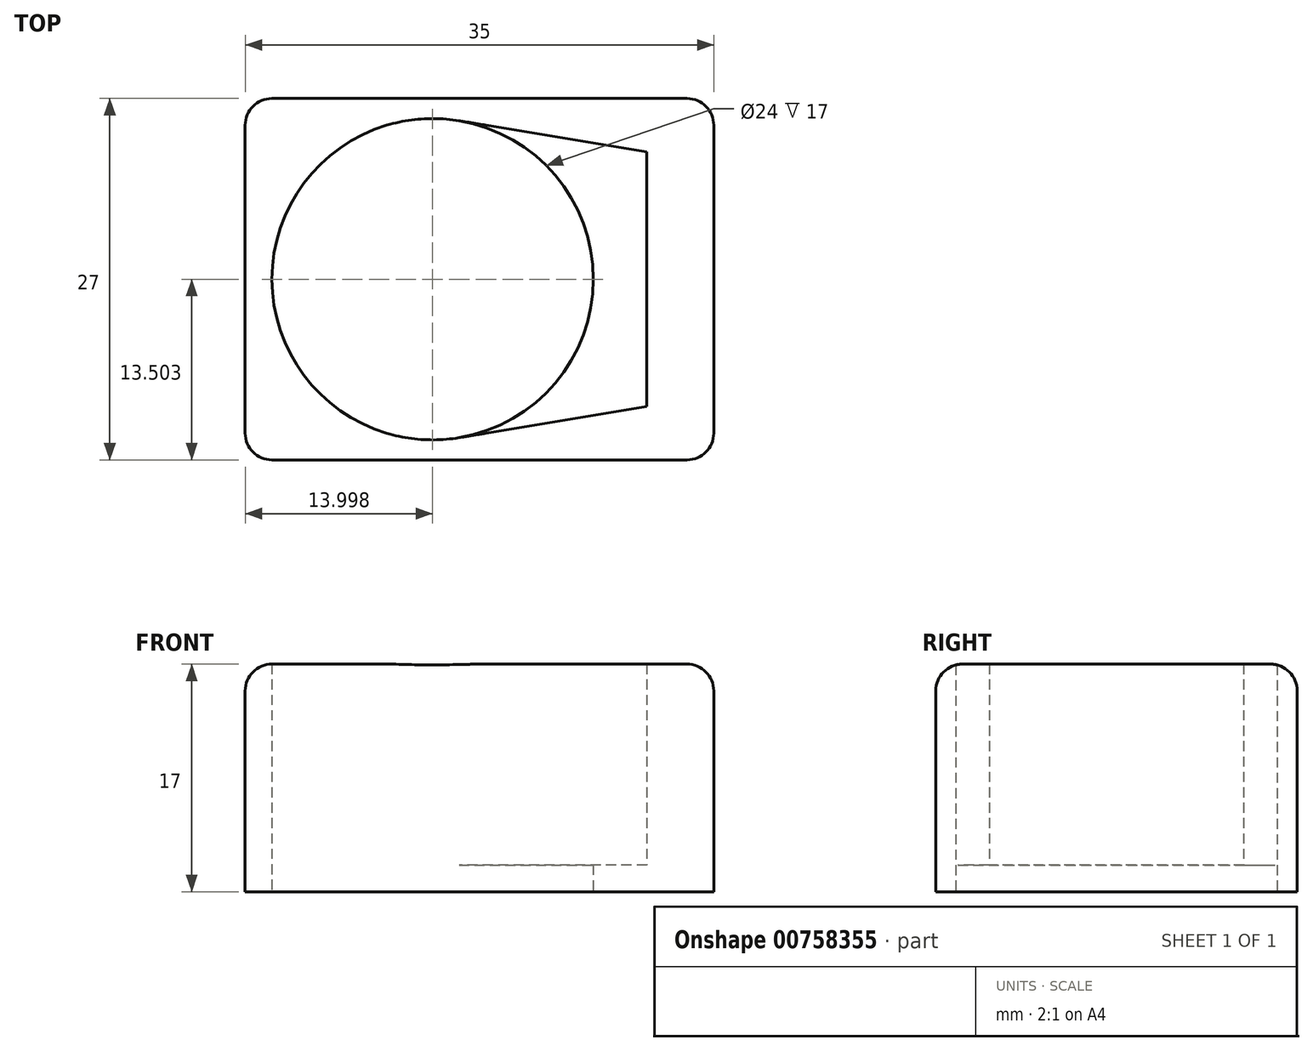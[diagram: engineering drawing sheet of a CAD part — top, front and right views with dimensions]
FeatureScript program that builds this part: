
annotation { "Feature Type Name" : "Feature", "Feature Type Description" : "" }
export const myFeature = defineFeature(function(context is Context, id is Id, definition is map)
    precondition{}
    {
        {
            var Q0;
            Q0=qCreatedBy(makeId("Top.planeOp"),FACE);
            var sketch = newSketch(context, id + "F0", { "sketchPlane" : qUnion([Q0])});
            skLineSegment(sketch, "E0", {"start": v(-0.7, 17.13) * mm, "end": v(-0.7, -1.87) * mm});
            skLineSegment(sketch, "E1", {"start": v(-0.7, 7.63) * mm, "end": v(-28.7, 7.63) * mm});
            skCircle(sketch, "E2", {"center": v(-16.7, 7.63) * mm, "radius": 12 * mm});
            skPoint(sketch, "E2.first.point", {"position": v(-8.44, 16.33) * mm});
            skPoint(sketch, "E2.third.point", {"position": v(-13.92, -4.04) * mm});
            skLineSegment(sketch, "E3", {"start": v(-0.7, 17.13) * mm, "end": v(-14.73, 19.47) * mm});
            skLineSegment(sketch, "E4", {"start": v(-0.7, -1.87) * mm, "end": v(-14.73, -4.2) * mm});
            skLineSegment(sketch, "E5.bottom", {"start": v(-30.7, 21.13) * mm, "end": v(4.3, 21.13) * mm});
            skLineSegment(sketch, "E5.top", {"start": v(-30.7, -5.87) * mm, "end": v(4.3, -5.87) * mm});
            skLineSegment(sketch, "E5.left", {"start": v(-30.7, 21.13) * mm, "end": v(-30.7, -5.87) * mm});
            skLineSegment(sketch, "E5.right", {"start": v(4.3, 21.13) * mm, "end": v(4.3, -5.87) * mm});
            skPoint(sketch, "E6", {"position": v(-28.7, 7.63) * mm});
            skPoint(sketch, "E7", {"position": v(-30.7, 7.63) * mm});
            skSolve(sketch);
        }
        {
            var Q0;
            {var subQ6=sQuery(id+"F0.wireOp",EDGE,"E3");Q0=makeQuery(id+"F0.imprint","IMPRINT",FACE,{"disambiguationData":[TD([[makeQuery(id+"F0.imprint","IMPRINT",EDGE,{"derivedFrom":subQ6}),-1.0]])]});}
            extrude(context, id + "F1", {"entities" : qUnion([Q0]), "depth" : 15 * mm, "offsetDistance" : 25 * mm});
        }
        {
            var Q0;
            {var subQ6=sQuery(id+"F0.wireOp",EDGE,"E3");Q0=makeQuery(id+"F0.imprint","IMPRINT",FACE,{"disambiguationData":[TD([[makeQuery(id+"F0.imprint","IMPRINT",EDGE,{"derivedFrom":subQ6}),-1.0]])]});}
            var Q1;
            {var subQ0=sQuery(id+"F0.wireOp",EDGE,"E2");var subQ1=sQuery(id+"F0.wireOp",EDGE,"E1");var subQ2=makeQuery(id+"F0.imprint","INTERSECT",VERTEX,{"disambiguationData":[OD(0.0)],"derivedFrom":[subQ1,subQ0]});Q1=makeQuery(id+"F0.imprint","IMPRINT",FACE,{"disambiguationData":[TD([[makeQuery(id+"F0.imprint","IMPRINT",EDGE,{"disambiguationData":[TD([[subQ2,1.0]])],"derivedFrom":subQ1}),1.0]])]});}
            var Q2;
            {var subQ0=sQuery(id+"F0.wireOp",EDGE,"E2");var subQ1=sQuery(id+"F0.wireOp",EDGE,"E1");var subQ2=makeQuery(id+"F0.imprint","INTERSECT",VERTEX,{"disambiguationData":[OD(0.0)],"derivedFrom":[subQ1,subQ0]});Q2=makeQuery(id+"F0.imprint","IMPRINT",FACE,{"disambiguationData":[TD([[makeQuery(id+"F0.imprint","IMPRINT",EDGE,{"disambiguationData":[TD([[subQ2,1.0]])],"derivedFrom":subQ1}),-1.0]])]});}
            var Q3;
            {var subQ0=sQuery(id+"F0.wireOp",EDGE,"E3");Q3=makeQuery(id+"F0.imprint","IMPRINT",FACE,{"disambiguationData":[TD([[makeQuery(id+"F0.imprint","IMPRINT",EDGE,{"derivedFrom":subQ0}),1.0]])]});}
            var Q4;
            {var subQ0=sQuery(id+"F0.wireOp",EDGE,"E4");Q4=makeQuery(id+"F0.imprint","IMPRINT",FACE,{"disambiguationData":[TD([[makeQuery(id+"F0.imprint","IMPRINT",EDGE,{"derivedFrom":subQ0}),-1.0]])]});}
            extrude(context, id + "F2", {"entities" : qUnion([Q0, Q1, Q2, Q3, Q4]), "operationType" : NewBodyOperationType.ADD, "depth" : -2 * mm, "offsetDistance" : 25 * mm});
        }
        {
            var Q0;
            {var subQ0=sQuery(id+"F0.wireOp",EDGE,"E5.left");var subQ1=sQuery(id+"F0.wireOp",EDGE,"E5.top");Q0=makeQuery(id+"F2.boolean.opBoolean","MERGE",EDGE,{"derivedFrom":[makeQuery(id+"F1.opExtrude","SWEPT_EDGE",EDGE,{"disambiguationData":[OSD([subQ1,subQ0])]}),makeQuery(id+"F2.opExtrude","SWEPT_EDGE",EDGE,{"disambiguationData":[OSD([subQ1,subQ0])]})]});}
            var Q1;
            Q1=makeQuery(id+"F1.opExtrude","CAP_EDGE",EDGE,{"disambiguationData":[OSD([sQuery(id+"F0.wireOp",EDGE,"E5.left")])],"isStart":false});
            var Q2;
            {var subQ0=sQuery(id+"F0.wireOp",EDGE,"E5.left");var subQ1=sQuery(id+"F0.wireOp",EDGE,"E5.bottom");Q2=makeQuery(id+"F2.boolean.opBoolean","MERGE",EDGE,{"derivedFrom":[makeQuery(id+"F1.opExtrude","SWEPT_EDGE",EDGE,{"disambiguationData":[OSD([subQ1,subQ0])]}),makeQuery(id+"F2.opExtrude","SWEPT_EDGE",EDGE,{"disambiguationData":[OSD([subQ1,subQ0])]})]});}
            var Q3;
            Q3=makeQuery(id+"F1.opExtrude","CAP_EDGE",EDGE,{"disambiguationData":[OSD([sQuery(id+"F0.wireOp",EDGE,"E5.bottom")])],"isStart":false});
            var Q4;
            Q4=makeQuery(id+"F1.opExtrude","CAP_EDGE",EDGE,{"disambiguationData":[OSD([sQuery(id+"F0.wireOp",EDGE,"E5.right")])],"isStart":false});
            var Q5;
            Q5=makeQuery(id+"F1.opExtrude","CAP_EDGE",EDGE,{"disambiguationData":[OSD([sQuery(id+"F0.wireOp",EDGE,"E5.top")])],"isStart":false});
            var Q6;
            {var subQ0=sQuery(id+"F0.wireOp",EDGE,"E5.right");var subQ1=sQuery(id+"F0.wireOp",EDGE,"E5.top");Q6=makeQuery(id+"F2.boolean.opBoolean","MERGE",EDGE,{"derivedFrom":[makeQuery(id+"F1.opExtrude","SWEPT_EDGE",EDGE,{"disambiguationData":[OSD([subQ1,subQ0])]}),makeQuery(id+"F2.opExtrude","SWEPT_EDGE",EDGE,{"disambiguationData":[OSD([subQ1,subQ0])]})]});}
            var Q7;
            {var subQ0=sQuery(id+"F0.wireOp",EDGE,"E5.right");var subQ1=sQuery(id+"F0.wireOp",EDGE,"E5.bottom");Q7=makeQuery(id+"F2.boolean.opBoolean","MERGE",EDGE,{"derivedFrom":[makeQuery(id+"F1.opExtrude","SWEPT_EDGE",EDGE,{"disambiguationData":[OSD([subQ1,subQ0])]}),makeQuery(id+"F2.opExtrude","SWEPT_EDGE",EDGE,{"disambiguationData":[OSD([subQ1,subQ0])]})]});}
            fillet(context, id + "F3", {"entities" : qUnion([Q0, Q1, Q2, Q3, Q4, Q5, Q6, Q7]), "radius" : 2 * mm, "tangentPropagation" : true, "allowEdgeOverflow" : false});
        }
    });
